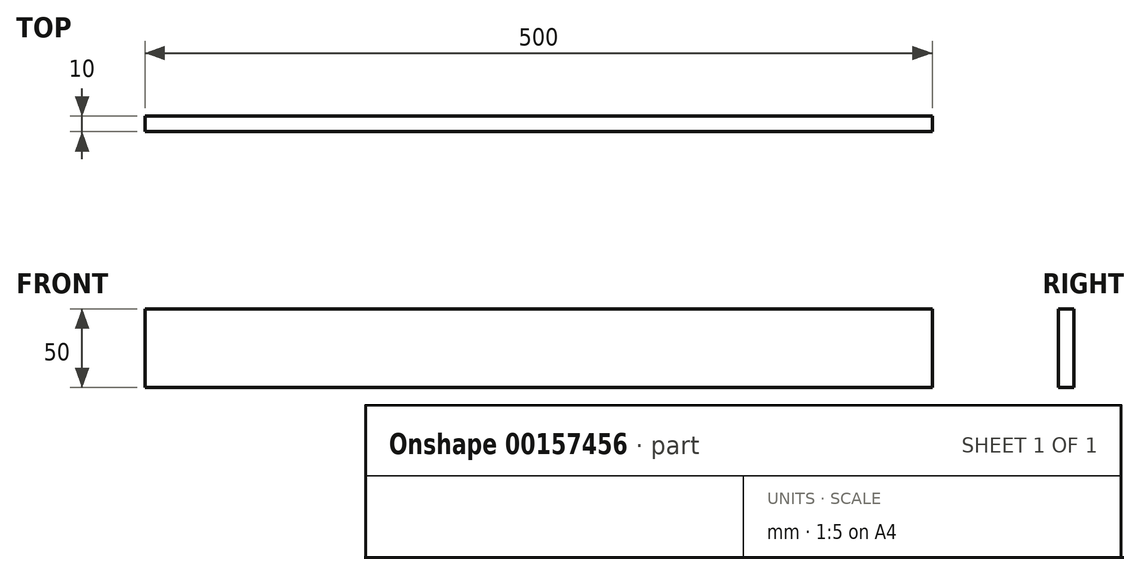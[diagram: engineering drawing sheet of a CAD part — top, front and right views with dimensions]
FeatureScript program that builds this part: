
annotation { "Feature Type Name" : "Feature", "Feature Type Description" : "" }
export const myFeature = defineFeature(function(context is Context, id is Id, definition is map)
    precondition{}
    {
        {
            var Q0;
            Q0=qCreatedBy(makeId("Front.planeOp"),FACE);
            var sketch = newSketch(context, id + "F0", { "sketchPlane" : qUnion([Q0])});
            skLineSegment(sketch, "E0.bottom", {"start": v(250, -25) * mm, "end": v(-250, -25) * mm});
            skLineSegment(sketch, "E0.top", {"start": v(250, 25) * mm, "end": v(-250, 25) * mm});
            skLineSegment(sketch, "E0.left", {"start": v(250, -25) * mm, "end": v(250, 25) * mm});
            skLineSegment(sketch, "E0.right", {"start": v(-250, -25) * mm, "end": v(-250, 25) * mm});
            skPoint(sketch, "E0.middle", {"position": v(0, 0) * mm});
            skSolve(sketch);
        }
        {
            var Q0;
            Q0=makeQuery(id+"F0.imprint","IMPRINT",FACE,{"disambiguationData":[TD([[makeQuery(id+"F0.imprint","IMPRINT",EDGE,{"derivedFrom":sQuery(id+"F0.wireOp",EDGE,"E0.bottom")}),-1.0]])]});
            extrude(context, id + "F1", {"entities" : qUnion([Q0]), "depth" : 10 * mm});
        }
    });
